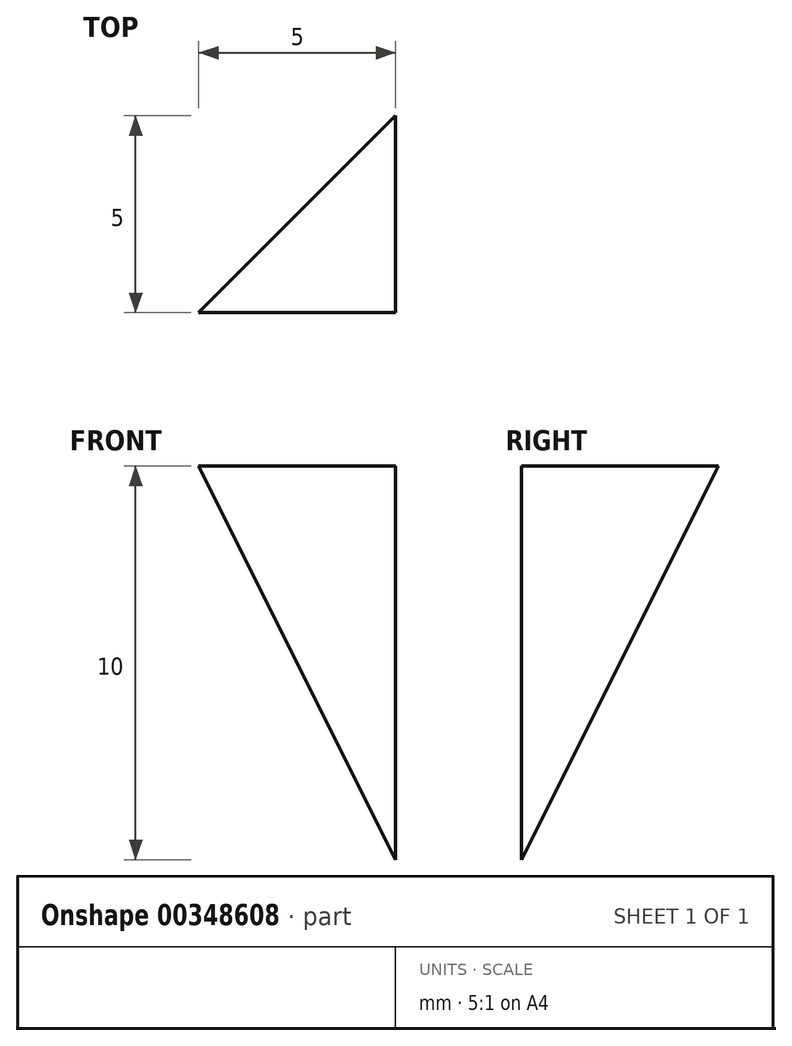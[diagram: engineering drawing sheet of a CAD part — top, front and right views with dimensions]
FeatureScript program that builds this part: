
annotation { "Feature Type Name" : "Feature", "Feature Type Description" : "" }
export const myFeature = defineFeature(function(context is Context, id is Id, definition is map)
    precondition{}
    {
        {
            var Q0;
            Q0=qCreatedBy(makeId("Front.planeOp"),FACE);
            var sketch = newSketch(context, id + "F0", { "sketchPlane" : qUnion([Q0])});
            skLineSegment(sketch, "E0.bottom", {"start": v(5, -5) * mm, "end": v(-5, -5) * mm});
            skLineSegment(sketch, "E0.top", {"start": v(5, 5) * mm, "end": v(-5, 5) * mm});
            skLineSegment(sketch, "E0.left", {"start": v(5, -5) * mm, "end": v(5, 5) * mm});
            skLineSegment(sketch, "E0.right", {"start": v(-5, -5) * mm, "end": v(-5, 5) * mm});
            skPoint(sketch, "E0.middle", {"position": v(0, 0) * mm});
            skSolve(sketch);
        }
        {
            var Q0;
            Q0=qSketchRegion(id+"F0",true);
            extrude(context, id + "F1", {"entities" : qUnion([Q0]), "endBound" : BoundingType.SYMMETRIC, "depth" : 10 * mm});
        }
        {
            var Q0;
            Q0=makeQuery(id+"F1.opExtrude","CAP_FACE",FACE,{"disambiguationData":[OSD([sQuery(id+"F0.wireOp",EDGE,"E0.bottom"),sQuery(id+"F0.wireOp",EDGE,"E0.top"),sQuery(id+"F0.wireOp",EDGE,"E0.left"),sQuery(id+"F0.wireOp",EDGE,"E0.right")])],"isStart":false});
            var sketch = newSketch(context, id + "F2", { "sketchPlane" : qUnion([Q0])});
            skLineSegment(sketch, "E1", {"start": v(0, 5) * mm, "end": v(5, -5) * mm});
            skSolve(sketch);
        }
        {
            var Q0;
            Q0=makeQuery(id+"F1.opExtrude","SWEPT_FACE",FACE,{"disambiguationData":[OSD([sQuery(id+"F0.wireOp",EDGE,"E0.left")])]});
            var sketch = newSketch(context, id + "F3", { "sketchPlane" : qUnion([Q0])});
            skLineSegment(sketch, "E2", {"start": v(0, 5) * mm, "end": v(-5, -5) * mm});
            skSolve(sketch);
        }
        {
            var Q0;
            Q0=makeQuery(id+"F1.opExtrude","SWEPT_FACE",FACE,{"disambiguationData":[OSD([sQuery(id+"F0.wireOp",EDGE,"E0.top")])]});
            var sketch = newSketch(context, id + "F4", { "sketchPlane" : qUnion([Q0])});
            skLineSegment(sketch, "E3", {"start": v(0, -5) * mm, "end": v(5, 0) * mm});
            skSolve(sketch);
        }
        {
            var Q0;
            Q0=sQuery(id+"F4.wireOp",VERTEX,"E3.start");
            var Q1;
            Q1=sQuery(id+"F4.wireOp",VERTEX,"E3.end");
            var Q2;
            Q2=sQuery(id+"F2.wireOp",VERTEX,"E1.end");
            cPlane(context, id + "F5", {"entities" : qUnion([Q0, Q1, Q2]), "cplaneType" : CPlaneType.THREE_POINT, "offset" : 25 * mm, "width" : 150 * mm, "height" : 150 * mm});
        }
        {
            var Q0;
            Q0=qCreatedBy(id+"F5.planeOp",FACE);
            var sketch = newSketch(context, id + "F6", { "sketchPlane" : qUnion([Q0])});
            skLineSegment(sketch, "E4.bottom", {"start": v(-12.41, 13.4) * mm, "end": v(11.11, 13.4) * mm});
            skLineSegment(sketch, "E4.top", {"start": v(-12.41, -14.84) * mm, "end": v(11.11, -14.84) * mm});
            skLineSegment(sketch, "E4.left", {"start": v(-12.41, 13.4) * mm, "end": v(-12.41, -14.84) * mm});
            skLineSegment(sketch, "E4.right", {"start": v(11.11, 13.4) * mm, "end": v(11.11, -14.84) * mm});
            skSolve(sketch);
        }
        {
            var Q0;
            Q0 = qSketchRegion(id + "F6", true);
            extrude(context, id + "F7", {"entities" : qUnion([Q0]), "operationType" : NewBodyOperationType.REMOVE, "endBound" : BoundingType.THROUGH_ALL, "oppositeDirection" : true, "depth" : 25 * mm});
        }
        {
            var Q0;
            Q0=qCreatedBy(id+"F5.planeOp",FACE);
            var sketch = newSketch(context, id + "F8", { "sketchPlane" : qUnion([Q0])});
            skPoint(sketch, "E5.0", {"position": v(-0.75, 2.24) * mm});
            skSolve(sketch);
        }
        {
            var Q0;
            Q0=sQuery(id+"F8.wireOp",VERTEX,"E5.0");
            var Q1;
            Q1=makeQuery(id+"F1.opExtrude","CAP_VERTEX",VERTEX,{"disambiguationData":[OSD([sQuery(id+"F0.wireOp",EDGE,"E0.top"),sQuery(id+"F0.wireOp",EDGE,"E0.left")])],"isStart":false});
            var Q2;
            Q2=sQuery(id+"F2.wireOp",VERTEX,"E1.end");
            cPlane(context, id + "F9", {"entities" : qUnion([Q0, Q1, Q2]), "cplaneType" : CPlaneType.THREE_POINT, "offset" : 25 * mm, "width" : 150 * mm, "height" : 150 * mm});
        }
    });
